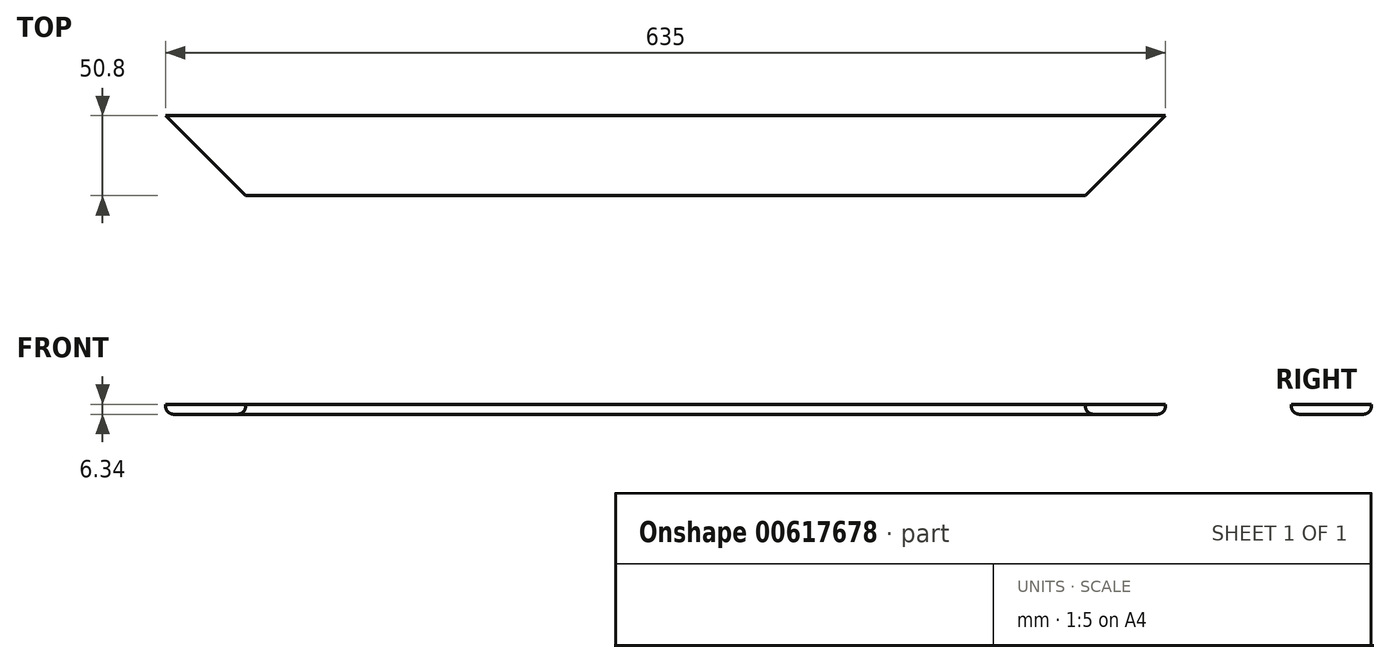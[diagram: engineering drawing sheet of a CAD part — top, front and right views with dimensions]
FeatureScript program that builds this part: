
annotation { "Feature Type Name" : "Feature", "Feature Type Description" : "" }
export const myFeature = defineFeature(function(context is Context, id is Id, definition is map)
    precondition{}
    {
        {
            var Q0;
            Q0=qCreatedBy(makeId("Top.planeOp"),FACE);
            var sketch = newSketch(context, id + "F0", { "sketchPlane" : qUnion([Q0])});
            skLineSegment(sketch, "E0", {"start": v(-307.1, 0) * mm, "end": v(327.9, 0) * mm});
            skLineSegment(sketch, "E1", {"start": v(-256.3, -50.8) * mm, "end": v(277.1, -50.8) * mm});
            skLineSegment(sketch, "E2", {"start": v(-307.1, 0) * mm, "end": v(-256.3, -50.8) * mm});
            skLineSegment(sketch, "E3", {"start": v(277.1, -50.8) * mm, "end": v(327.9, 0) * mm});
            skSolve(sketch);
        }
        {
            var Q0;
            Q0=makeQuery(id+"F0.imprint","IMPRINT",FACE,{"disambiguationData":[TD([[makeQuery(id+"F0.imprint","IMPRINT",EDGE,{"derivedFrom":sQuery(id+"F0.wireOp",EDGE,"E0")}),-1.0]])]});
            extrude(context, id + "F1", {"entities" : qUnion([Q0]), "endBound" : BoundingType.SYMMETRIC, "depth" : 6.35 * mm, "offsetDistance" : 25.4 * mm});
        }
        {
            var Q0;
            Q0=makeQuery(id+"F1.opExtrude","CAP_EDGE",EDGE,{"disambiguationData":[OSD([sQuery(id+"F0.wireOp",EDGE,"E0")])],"isStart":true});
            var Q1;
            Q1=makeQuery(id+"F1.opExtrude","CAP_EDGE",EDGE,{"disambiguationData":[OSD([sQuery(id+"F0.wireOp",EDGE,"E1")])],"isStart":true});
            fillet(context, id + "F2", {"entities" : qUnion([Q0, Q1]), "radius" : 5.08 * mm, "tangentPropagation" : true, "allowEdgeOverflow" : false});
        }
    });
